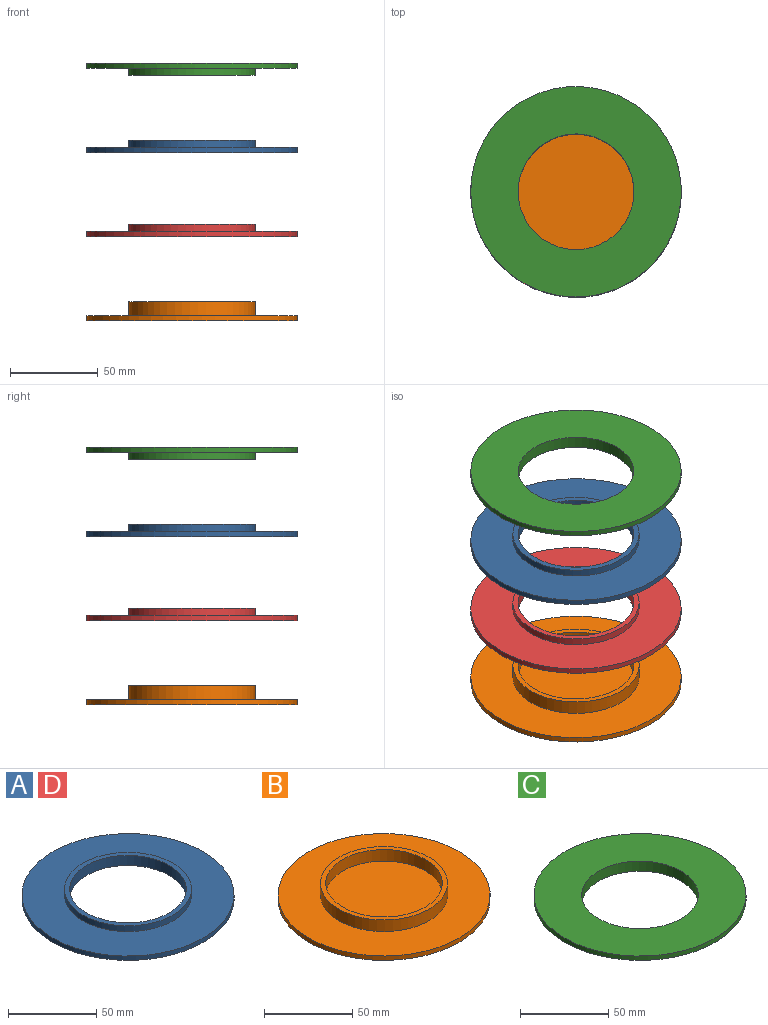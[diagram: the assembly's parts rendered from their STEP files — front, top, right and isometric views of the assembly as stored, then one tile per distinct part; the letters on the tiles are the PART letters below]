
ASSEMBLY  parts=4 mates=4
PART A: 6 faces, bbox 120x120x7 mm
  f0: plane 72x72mm, normal (0,0,1), area 650.3mm2, adj f1,f5
  f1: cylinder r=33mm len=66mm, axis (0,0,-1), area 1451.4mm2, adj f0,f2
  f2: plane 120x120mm, normal (0,0,-1), area 7888.5mm2, adj f1,f3
  f3: cylinder r=60mm len=120mm, axis (0,0,-1), area 1131mm2, adj f2,f4
  f4: plane 120x120mm, normal (0,0,1), area 7238.2mm2, adj f3,f5
  f5: cylinder r=36mm len=72mm, axis (0,0,-1), area 904.8mm2, adj f0,f4
PART B: 7 faces, bbox 120x120x11 mm
  f0: cylinder r=60mm len=120mm, axis (0,0,1), area 1131mm2, adj f1,f6
  f1: plane 120x120mm, normal (0,0,1), area 7238.2mm2, adj f0,f2
  f2: cylinder r=36mm len=72mm, axis (0,0,1), area 1809.6mm2, adj f1,f3
  f3: plane 72x72mm, normal (0,0,1), area 650.3mm2, adj f2,f4
  f4: cylinder r=33mm len=66mm, axis (0,0,1), area 1658.8mm2, adj f3,f5
  f5: plane 66x66mm, normal (0,0,1), area 3421.2mm2, adj f4
  f6: plane 120x120mm, normal (0,0,-1), area 11309.7mm2, adj f0
PART C: 6 faces, bbox 120x120x7 mm
  f0: plane 120x120mm, normal (0,0,1), area 7888.5mm2, adj f1,f5
  f1: cylinder r=33mm len=66mm, axis (0,0,-1), area 1451.4mm2, adj f0,f2
  f2: plane 72x72mm, normal (0,0,-1), area 650.3mm2, adj f1,f3
  f3: cylinder r=36mm len=72mm, axis (0,0,-1), area 904.8mm2, adj f2,f4
  f4: plane 120x120mm, normal (0,0,-1), area 7238.2mm2, adj f3,f5
  f5: cylinder r=60mm len=120mm, axis (0,0,-1), area 1131mm2, adj f0,f4
PART D: same geometry as A
PLACE A t=(0,0,93)mm
PLACE B t=(0,0,-3)mm
PLACE C t=(0,0,141)mm
PLACE D t=(0,0,45)mm
MATE slider B.f0 <-> C.f1  axis (0,0,1) through (0,0,4)mm
MATE parallel C.f1 <-> A.f1  axis (0,0,-1) through (0,0,141)mm
MATE slider B.f0 <-> D.f1  axis (0,0,1) through (0,0,4)mm
MATE parallel D.f1 <-> B.f0  axis (0,0,-1) through (0,0,45)mm
